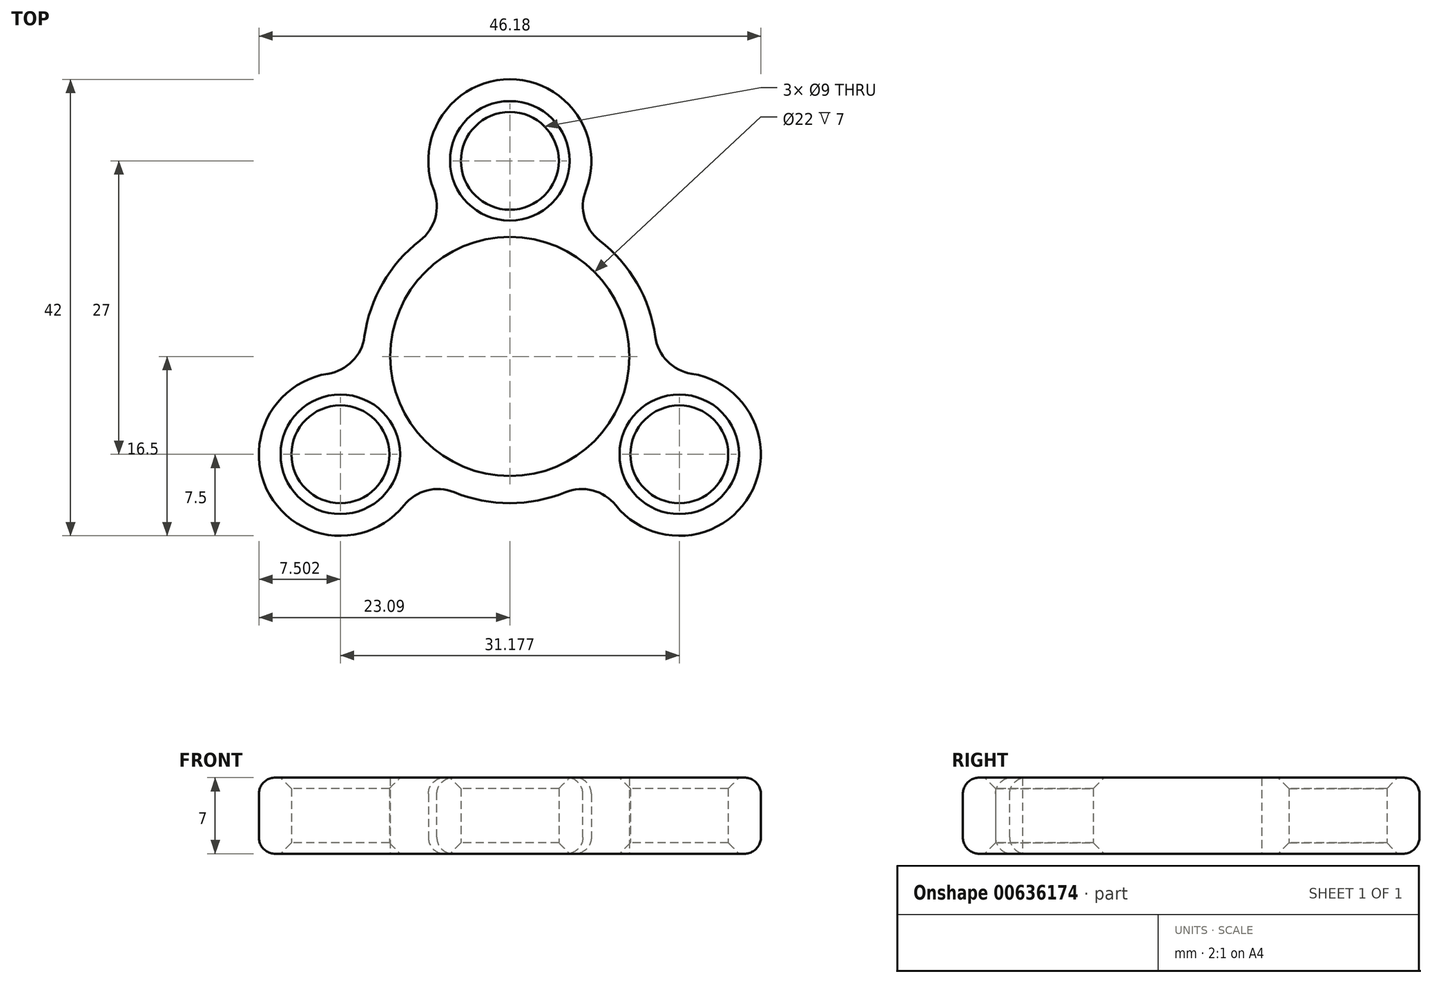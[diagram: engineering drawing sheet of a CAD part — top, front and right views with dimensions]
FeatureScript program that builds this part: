
annotation { "Feature Type Name" : "Feature", "Feature Type Description" : "" }
export const myFeature = defineFeature(function(context is Context, id is Id, definition is map)
    precondition{}
    {
        {
            var Q0;
            Q0=qCreatedBy(makeId("Top.planeOp"),FACE);
            var sketch = newSketch(context, id + "F0", { "sketchPlane" : qUnion([Q0])});
            skCircle(sketch, "E0", {"center": v(0, 0) * mm, "radius": 11 * mm});
            skCircle(sketch, "E1", {"center": v(0, 0) * mm, "radius": 13.5 * mm});
            skCircle(sketch, "E2", {"center": v(0, 18) * mm, "radius": 4.5 * mm});
            skCircle(sketch, "E3", {"center": v(0, 18) * mm, "radius": 7.5 * mm});
            skCircle(sketch, "E4.1.0", {"center": v(-15.59, -9) * mm, "radius": 7.5 * mm});
            skCircle(sketch, "E4.1.1", {"center": v(-15.59, -9) * mm, "radius": 4.5 * mm});
            skCircle(sketch, "E4.2.0", {"center": v(15.59, -9) * mm, "radius": 7.5 * mm});
            skCircle(sketch, "E4.2.1", {"center": v(15.59, -9) * mm, "radius": 4.5 * mm});
            skSolve(sketch);
        }
        {
            var Q0;
            {var subQ0=sQuery(id+"F0.wireOp",EDGE,"E2");Q0=makeQuery(id+"F0.imprint","IMPRINT",FACE,{"disambiguationData":[TD([[makeQuery(id+"F0.imprint","IMPRINT",EDGE,{"derivedFrom":subQ0}),-1.0]])]});}
            var Q1;
            Q1=makeQuery(id+"F0.imprint","IMPRINT",FACE,{"disambiguationData":[TD([[makeQuery(id+"F0.imprint","IMPRINT",EDGE,{"derivedFrom":sQuery(id+"F0.wireOp",EDGE,"E0")}),-1.0]])]});
            var Q2;
            {var subQ3=sQuery(id+"F0.wireOp",EDGE,"E4.1.1");Q2=makeQuery(id+"F0.imprint","IMPRINT",FACE,{"disambiguationData":[TD([[makeQuery(id+"F0.imprint","IMPRINT",EDGE,{"derivedFrom":subQ3}),-1.0]])]});}
            var Q3;
            {var subQ0=sQuery(id+"F0.wireOp",EDGE,"E4.1.0");var subQ1=sQuery(id+"F0.wireOp",EDGE,"E1");var subQ2=makeQuery(id+"F0.imprint","INTERSECT",VERTEX,{"disambiguationData":[OD(0.0)],"derivedFrom":[subQ1,subQ0]});Q3=makeQuery(id+"F0.imprint","IMPRINT",FACE,{"disambiguationData":[TD([[makeQuery(id+"F0.imprint","IMPRINT",EDGE,{"disambiguationData":[TD([[subQ2,-1.0]])],"derivedFrom":subQ1}),1.0]])]});}
            var Q4;
            {var subQ0=sQuery(id+"F0.wireOp",EDGE,"E1");var subQ1=makeQuery(id+"F0.imprint","INTERSECT",VERTEX,{"derivedFrom":[subQ0,sQuery(id+"F0.wireOp",EDGE,"E2")]});Q4=makeQuery(id+"F0.imprint","IMPRINT",FACE,{"disambiguationData":[TD([[makeQuery(id+"F0.imprint","IMPRINT",EDGE,{"disambiguationData":[TD([[subQ1,1.0]])],"derivedFrom":subQ0}),1.0]])]});}
            var Q5;
            {var subQ3=sQuery(id+"F0.wireOp",EDGE,"E4.2.1");Q5=makeQuery(id+"F0.imprint","IMPRINT",FACE,{"disambiguationData":[TD([[makeQuery(id+"F0.imprint","IMPRINT",EDGE,{"derivedFrom":subQ3}),-1.0]])]});}
            var Q6;
            {var subQ0=sQuery(id+"F0.wireOp",EDGE,"E4.2.0");var subQ1=sQuery(id+"F0.wireOp",EDGE,"E1");var subQ2=makeQuery(id+"F0.imprint","INTERSECT",VERTEX,{"disambiguationData":[OD(0.0)],"derivedFrom":[subQ1,subQ0]});Q6=makeQuery(id+"F0.imprint","IMPRINT",FACE,{"disambiguationData":[TD([[makeQuery(id+"F0.imprint","IMPRINT",EDGE,{"disambiguationData":[TD([[subQ2,-1.0]])],"derivedFrom":subQ1}),1.0]])]});}
            extrude(context, id + "F1", {"entities" : qUnion([Q0, Q1, Q2, Q3, Q4, Q5, Q6]), "depth" : 7 * mm, "offsetDistance" : 25 * mm});
        }
        {
            var Q0;
            Q0=makeQuery(id+"F1.opExtrude","CAP_EDGE",EDGE,{"disambiguationData":[OSD([sQuery(id+"F0.wireOp",EDGE,"E2")])],"isStart":false});
            var Q1;
            Q1=makeQuery(id+"F1.opExtrude","CAP_EDGE",EDGE,{"disambiguationData":[OSD([sQuery(id+"F0.wireOp",EDGE,"E4.2.1")])],"isStart":false});
            var Q2;
            Q2=makeQuery(id+"F1.opExtrude","CAP_EDGE",EDGE,{"disambiguationData":[OSD([sQuery(id+"F0.wireOp",EDGE,"E4.1.1")])],"isStart":false});
            var Q3;
            Q3=makeQuery(id+"F1.opExtrude","CAP_EDGE",EDGE,{"disambiguationData":[OSD([sQuery(id+"F0.wireOp",EDGE,"E4.1.1")])],"isStart":true});
            var Q4;
            Q4=makeQuery(id+"F1.opExtrude","CAP_EDGE",EDGE,{"disambiguationData":[OSD([sQuery(id+"F0.wireOp",EDGE,"E2")])],"isStart":true});
            var Q5;
            Q5=makeQuery(id+"F1.opExtrude","CAP_EDGE",EDGE,{"disambiguationData":[OSD([sQuery(id+"F0.wireOp",EDGE,"E4.2.1")])],"isStart":true});
            chamfer(context, id + "F2", {"entities" : qUnion([Q0, Q1, Q2, Q3, Q4, Q5]), "width" : 1 * mm, "tangentPropagation" : true});
        }
        {
            var Q0;
            {var subQ0=sQuery(id+"F0.wireOp",EDGE,"E4.2.0");var subQ1=sQuery(id+"F0.wireOp",EDGE,"E1");Q0=makeQuery(id+"F1.opExtrude","SWEPT_EDGE",EDGE,{"disambiguationData":[OSD([subQ1,subQ0]),TDD([makeQuery(id+"F0.imprint","INTERSECT",VERTEX,{"disambiguationData":[OD(1.0)],"derivedFrom":[subQ1,subQ0]})])]});}
            var Q1;
            {var subQ0=sQuery(id+"F0.wireOp",EDGE,"E3");var subQ1=sQuery(id+"F0.wireOp",EDGE,"E1");Q1=makeQuery(id+"F1.opExtrude","SWEPT_EDGE",EDGE,{"disambiguationData":[OSD([subQ1,subQ0]),TDD([makeQuery(id+"F0.imprint","INTERSECT",VERTEX,{"disambiguationData":[OD(0.0)],"derivedFrom":[subQ1,subQ0]})])]});}
            var Q2;
            {var subQ0=sQuery(id+"F0.wireOp",EDGE,"E4.1.0");var subQ1=sQuery(id+"F0.wireOp",EDGE,"E1");Q2=makeQuery(id+"F1.opExtrude","SWEPT_EDGE",EDGE,{"disambiguationData":[OSD([subQ1,subQ0]),TDD([makeQuery(id+"F0.imprint","INTERSECT",VERTEX,{"disambiguationData":[OD(0.0)],"derivedFrom":[subQ1,subQ0]})])]});}
            var Q3;
            {var subQ0=sQuery(id+"F0.wireOp",EDGE,"E3");var subQ1=sQuery(id+"F0.wireOp",EDGE,"E1");Q3=makeQuery(id+"F1.opExtrude","SWEPT_EDGE",EDGE,{"disambiguationData":[OSD([subQ1,subQ0]),TDD([makeQuery(id+"F0.imprint","INTERSECT",VERTEX,{"disambiguationData":[OD(1.0)],"derivedFrom":[subQ1,subQ0]})])]});}
            var Q4;
            {var subQ0=sQuery(id+"F0.wireOp",EDGE,"E4.1.0");var subQ1=sQuery(id+"F0.wireOp",EDGE,"E1");Q4=makeQuery(id+"F1.opExtrude","SWEPT_EDGE",EDGE,{"disambiguationData":[OSD([subQ1,subQ0]),TDD([makeQuery(id+"F0.imprint","INTERSECT",VERTEX,{"disambiguationData":[OD(1.0)],"derivedFrom":[subQ1,subQ0]})])]});}
            var Q5;
            {var subQ0=sQuery(id+"F0.wireOp",EDGE,"E4.2.0");var subQ1=sQuery(id+"F0.wireOp",EDGE,"E1");Q5=makeQuery(id+"F1.opExtrude","SWEPT_EDGE",EDGE,{"disambiguationData":[OSD([subQ1,subQ0]),TDD([makeQuery(id+"F0.imprint","INTERSECT",VERTEX,{"disambiguationData":[OD(0.0)],"derivedFrom":[subQ1,subQ0]})])]});}
            fillet(context, id + "F3", {"entities" : qUnion([Q0, Q1, Q2, Q3, Q4, Q5]), "radius" : 4 * mm, "tangentPropagation" : true, "allowEdgeOverflow" : false});
        }
        {
            var Q0;
            Q0=makeQuery(id+"F1.opExtrude","CAP_EDGE",EDGE,{"disambiguationData":[OSD([sQuery(id+"F0.wireOp",EDGE,"E3")])],"isStart":false});
            var Q1;
            Q1=makeQuery(id+"F1.opExtrude","CAP_EDGE",EDGE,{"disambiguationData":[OSD([sQuery(id+"F0.wireOp",EDGE,"E3")])],"isStart":true});
            fillet(context, id + "F4", {"entities" : qUnion([Q0, Q1]), "radius" : 1.5 * mm, "tangentPropagation" : true, "allowEdgeOverflow" : false});
        }
    });
